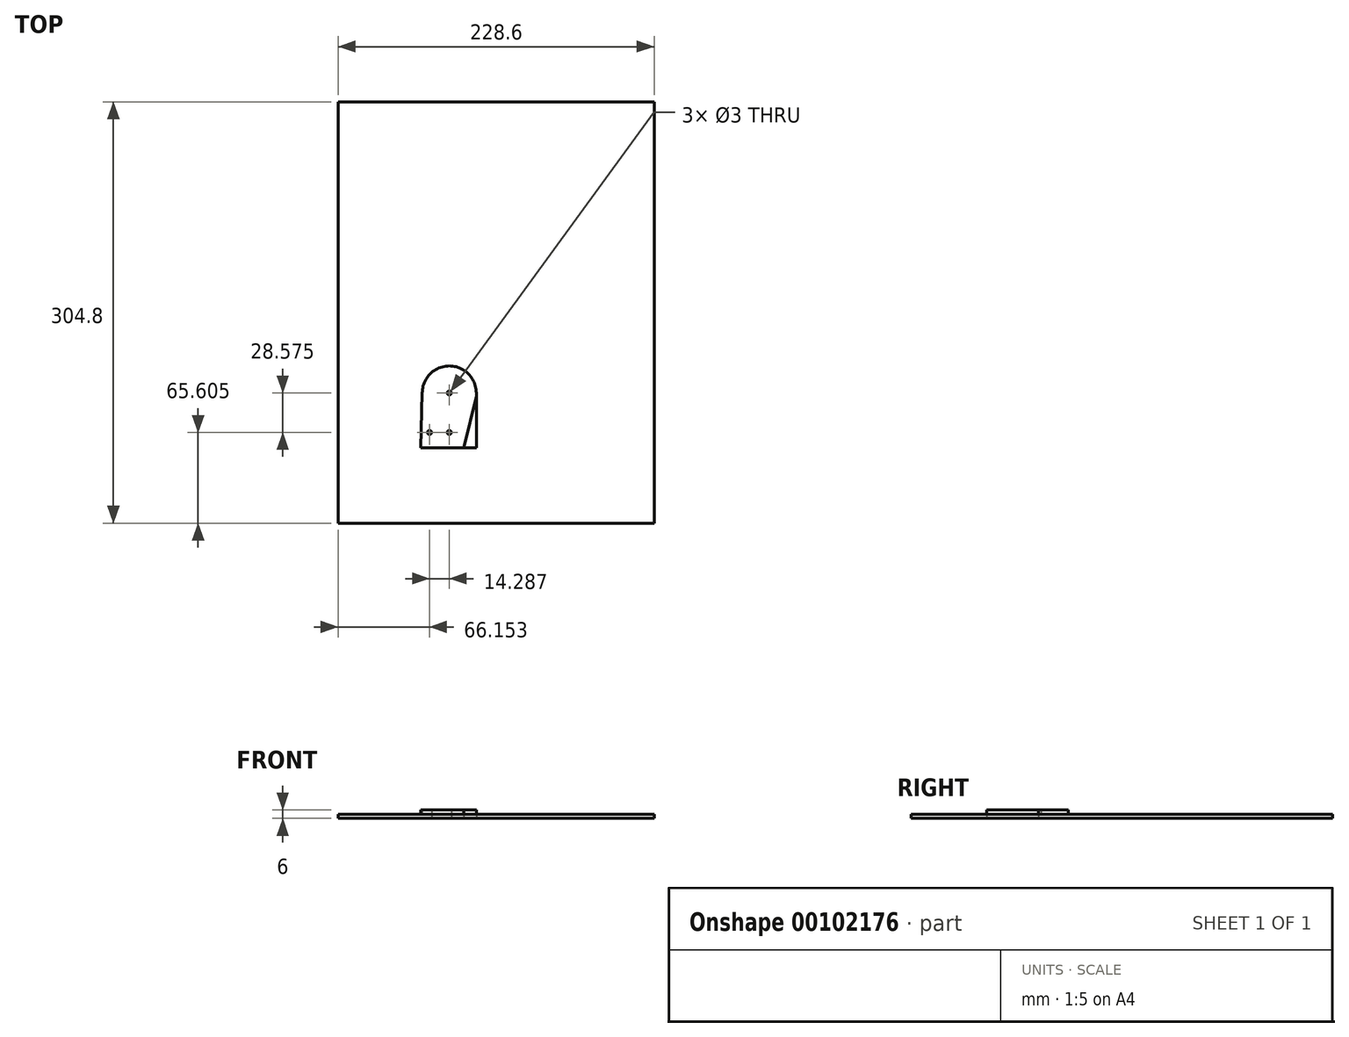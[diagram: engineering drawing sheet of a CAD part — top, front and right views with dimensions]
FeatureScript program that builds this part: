
annotation { "Feature Type Name" : "Feature", "Feature Type Description" : "" }
export const myFeature = defineFeature(function(context is Context, id is Id, definition is map)
    precondition{}
    {
        {
            var Q0;
            Q0=qCreatedBy(makeId("Top.planeOp"),FACE);
            var sketch = newSketch(context, id + "F0", { "sketchPlane" : qUnion([Q0])});
            skCircle(sketch, "E0", {"center": v(0, 19.59) * mm, "radius": 19.56 * mm});
            skLineSegment(sketch, "E1", {"start": v(0, 19.59) * mm, "end": v(19.56, 19.59) * mm});
            skLineSegment(sketch, "E2", {"start": v(19.56, 19.59) * mm, "end": v(19.56, -20.03) * mm});
            skLineSegment(sketch, "E3", {"start": v(0, 19.59) * mm, "end": v(0, -8.99) * mm});
            skLineSegment(sketch, "E4", {"start": v(19.56, -20.03) * mm, "end": v(-20.57, -20.03) * mm});
            skLineSegment(sketch, "E5", {"start": v(-19.56, 19.53) * mm, "end": v(-20.57, -20.03) * mm});
            skLineSegment(sketch, "E6", {"start": v(0, -5) * mm, "end": v(-14.29, -5) * mm});
            skLineSegment(sketch, "E7", {"start": v(-14.29, -8.99) * mm, "end": v(-14.29, -5) * mm});
            skCircle(sketch, "E8", {"center": v(0, 19.59) * mm, "radius": 1.5 * mm});
            skCircle(sketch, "E9", {"center": v(0, -8.99) * mm, "radius": 1.5 * mm});
            skCircle(sketch, "E10", {"center": v(-14.29, -8.99) * mm, "radius": 1.5 * mm});
            skLineSegment(sketch, "E11", {"start": v(10.54, -20.03) * mm, "end": v(19.56, 17.54) * mm});
            skLineSegment(sketch, "E12.bottom", {"start": v(-80.44, 230.2) * mm, "end": v(148.16, 230.2) * mm});
            skLineSegment(sketch, "E12.top", {"start": v(-80.44, -74.6) * mm, "end": v(148.16, -74.6) * mm});
            skLineSegment(sketch, "E12.left", {"start": v(-80.44, 230.2) * mm, "end": v(-80.44, -74.6) * mm});
            skLineSegment(sketch, "E12.right", {"start": v(148.16, 230.2) * mm, "end": v(148.16, -74.6) * mm});
            skSolve(sketch);
        }
        {
            var Q0;
            {var subQ0=sQuery(id+"F0.wireOp",EDGE,"E2");var subQ3=sQuery(id+"F0.wireOp",EDGE,"E11");var subQ5=makeQuery(id+"F0.imprint","INTERSECT",VERTEX,{"derivedFrom":[subQ0,subQ3]});Q0=makeQuery(id+"F0.imprint","IMPRINT",FACE,{"disambiguationData":[TD([[makeQuery(id+"F0.imprint","IMPRINT",EDGE,{"disambiguationData":[TD([[subQ5,1.0]])],"derivedFrom":subQ3}),1.0]])]});}
            var Q1;
            {var subQ1=sQuery(id+"F0.wireOp",EDGE,"E0");var subQ8=makeQuery(id+"F0.imprint","INTERSECT",VERTEX,{"derivedFrom":[subQ1,sQuery(id+"F0.wireOp",EDGE,"E5")]});Q1=makeQuery(id+"F0.imprint","IMPRINT",FACE,{"disambiguationData":[TD([[makeQuery(id+"F0.imprint","IMPRINT",EDGE,{"disambiguationData":[TD([[subQ8,-1.0]])],"derivedFrom":subQ1}),1.0]])]});}
            var Q2;
            {var subQ0=sQuery(id+"F0.wireOp",EDGE,"E5");Q2=makeQuery(id+"F0.imprint","IMPRINT",FACE,{"disambiguationData":[TD([[makeQuery(id+"F0.imprint","IMPRINT",EDGE,{"derivedFrom":subQ0}),1.0]])]});}
            var Q3;
            {var subQ0=sQuery(id+"F0.wireOp",EDGE,"E3");var subQ1=sQuery(id+"F0.wireOp",EDGE,"E0");var subQ2=makeQuery(id+"F0.imprint","INTERSECT",VERTEX,{"derivedFrom":[subQ1,subQ0]});Q3=makeQuery(id+"F0.imprint","IMPRINT",FACE,{"disambiguationData":[TD([[makeQuery(id+"F0.imprint","IMPRINT",EDGE,{"disambiguationData":[TD([[subQ2,-1.0]])],"derivedFrom":subQ1}),1.0]])]});}
            extrude(context, id + "F1", {"entities" : qUnion([Q0, Q1, Q2, Q3]), "depth" : 6 * mm});
        }
        {
            var Q0;
            {var subQ8=sQuery(id+"F0.wireOp",EDGE,"E5");Q0=makeQuery(id+"F0.imprint","IMPRINT",FACE,{"disambiguationData":[TD([[makeQuery(id+"F0.imprint","IMPRINT",EDGE,{"derivedFrom":subQ8}),-1.0]])]});}
            extrude(context, id + "F2", {"entities" : qUnion([Q0]), "operationType" : NewBodyOperationType.ADD, "depth" : 3 * mm});
        }
    });
